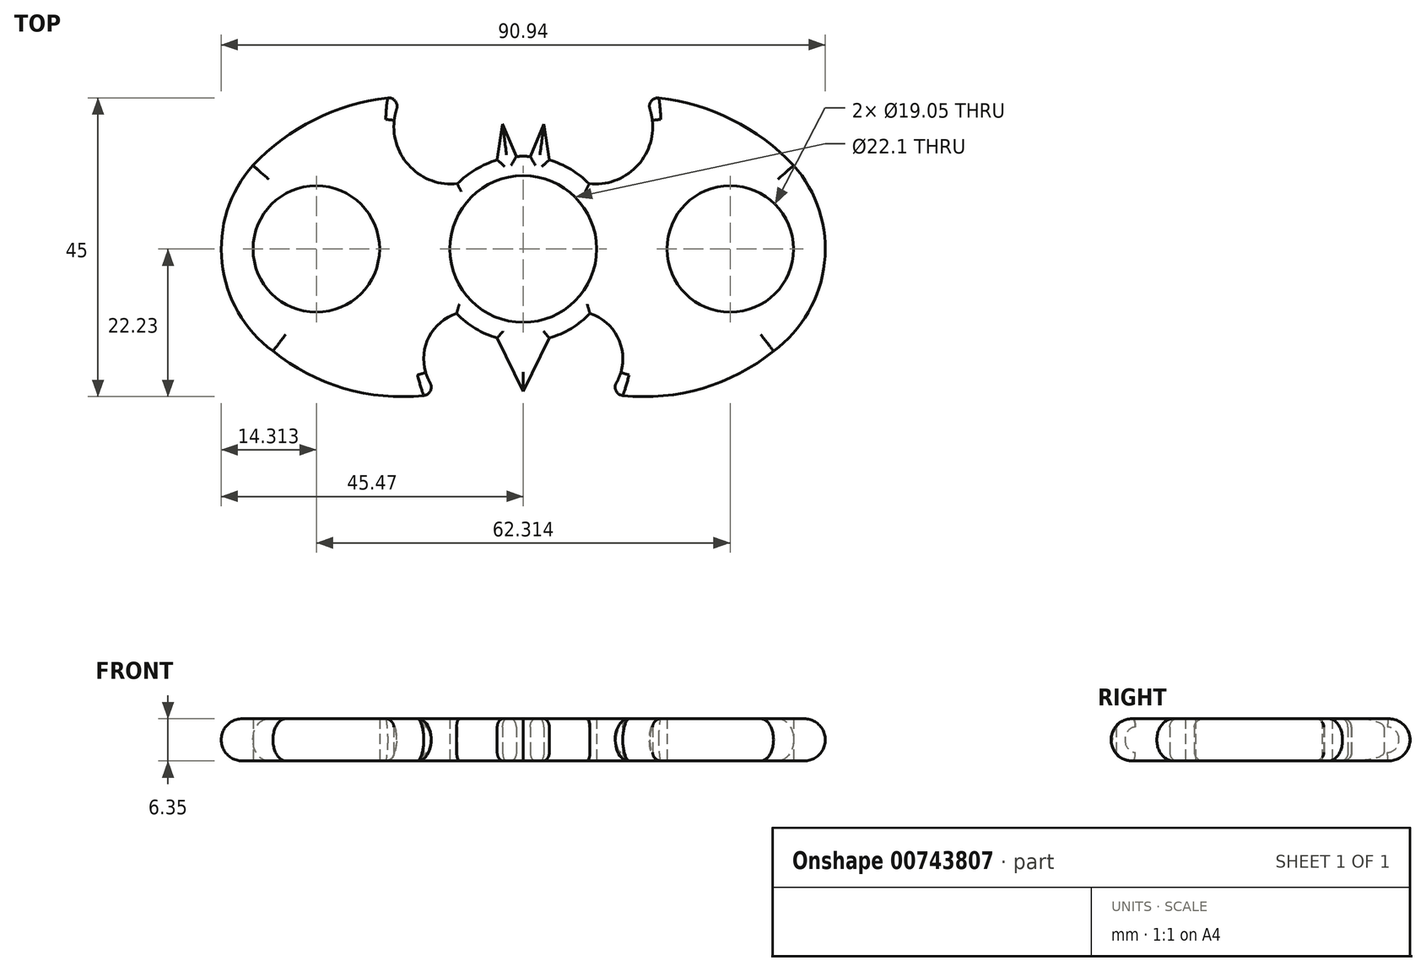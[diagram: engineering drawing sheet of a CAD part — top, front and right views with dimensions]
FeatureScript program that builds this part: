
annotation { "Feature Type Name" : "Feature", "Feature Type Description" : "" }
export const myFeature = defineFeature(function(context is Context, id is Id, definition is map)
    precondition{}
    {
        {
            var Q0;
            Q0=qCreatedBy(makeId("Top.planeOp"),FACE);
            var sketch = newSketch(context, id + "F0", { "sketchPlane" : qUnion([Q0])});
            skCircle(sketch, "E0", {"center": v(0, 0) * mm, "radius": 11.05 * mm});
            skCircle(sketch, "E1", {"center": v(0, 0) * mm, "radius": 13.97 * mm});
            skCircle(sketch, "E2", {"center": v(-31.16, 0) * mm, "radius": 9.53 * mm});
            skCircle(sketch, "E3", {"center": v(31.16, 0) * mm, "radius": 9.53 * mm});
            skArc(sketch, "E4", {"start": v(37.68, -15.37) * mm, "mid": v(45.36, -2.05) * mm, "end": v(40.7, 12.6) * mm});
            skArc(sketch, "E5", {"start": v(-18.2, 22.95) * mm, "mid": v(-30.45, 19.93) * mm, "end": v(-40.7, 12.6) * mm});
            skArc(sketch, "E6", {"start": v(-18.2, 22.95) * mm, "mid": v(-18.15, 13.81) * mm, "end": v(-9.93, 9.83) * mm});
            skArc(sketch, "E7.trimOffspring", {"start": v(-40.7, 12.6) * mm, "mid": v(-45.36, -2.05) * mm, "end": v(-37.68, -15.37) * mm});
            skArc(sketch, "E8.MirrorCS", {"start": v(18.2, 22.95) * mm, "mid": v(18.15, 13.81) * mm, "end": v(9.93, 9.83) * mm});
            skArc(sketch, "E9.MirrorCS", {"start": v(18.2, 22.95) * mm, "mid": v(30.45, 19.93) * mm, "end": v(40.7, 12.6) * mm});
            skArc(sketch, "E10", {"start": v(-37.68, -15.37) * mm, "mid": v(-25.91, -21.27) * mm, "end": v(-12.76, -21.74) * mm});
            skArc(sketch, "E11", {"start": v(-10.03, -9.72) * mm, "mid": v(-14.81, -14.95) * mm, "end": v(-12.76, -21.74) * mm});
            skArc(sketch, "E12.MirrorCS", {"start": v(10.03, -9.72) * mm, "mid": v(14.81, -14.95) * mm, "end": v(12.76, -21.74) * mm});
            skArc(sketch, "E13.MirrorCS", {"start": v(37.68, -15.37) * mm, "mid": v(25.91, -21.27) * mm, "end": v(12.76, -21.74) * mm});
            skPoint(sketch, "E14.end.orphan", {"position": v(2.34, 18.82) * mm});
            skPoint(sketch, "E15.orphan", {"position": v(3.92, 13.4) * mm});
            skPoint(sketch, "E16.end.orphan", {"position": v(-1.04, 13.93) * mm});
            skPoint(sketch, "E17.end.orphan", {"position": v(-2.23, 18.82) * mm});
            skPoint(sketch, "E18.MirrorCS.end.orphan", {"position": v(1.04, 13.93) * mm});
            skPoint(sketch, "E18.MirrorCS.start.orphan", {"position": v(2.23, 18.82) * mm});
            skPoint(sketch, "E19.end.orphan", {"position": v(-4.8, 18.35) * mm});
            skPoint(sketch, "E20.MirrorCS.end.orphan", {"position": v(4.8, 18.35) * mm});
            skLineSegment(sketch, "E21", {"start": v(-1.04, 13.93) * mm, "end": v(-3.1, 18.83) * mm});
            skLineSegment(sketch, "E22", {"start": v(-3.1, 18.83) * mm, "end": v(-3.92, 13.4) * mm});
            skLineSegment(sketch, "E23.MirrorCS", {"start": v(1.04, 13.93) * mm, "end": v(3.1, 18.83) * mm});
            skLineSegment(sketch, "E24.MirrorCS", {"start": v(3.1, 18.83) * mm, "end": v(3.92, 13.4) * mm});
            skPoint(sketch, "E25.end.orphan", {"position": v(0, -21.45) * mm});
            skPoint(sketch, "E25.start.orphan", {"position": v(-4.01, -13.38) * mm});
            skPoint(sketch, "E26.MirrorCS.start.orphan", {"position": v(4.01, -13.38) * mm});
            skPoint(sketch, "E27.MirrorCS.end.orphan", {"position": v(-3.92, -13.4) * mm});
            skPoint(sketch, "E27.MirrorCS.start.orphan", {"position": v(-3.1, -18.83) * mm});
            skLineSegment(sketch, "E28", {"start": v(-3.92, -13.4) * mm, "end": v(0, -21.45) * mm});
            skLineSegment(sketch, "E29.MirrorCS", {"start": v(3.92, -13.4) * mm, "end": v(0, -21.45) * mm});
            skLineSegment(sketch, "E30", {"start": v(-26.42, 0) * mm, "end": v(-31.16, 0) * mm});
            skLineSegment(sketch, "E31", {"start": v(26.42, 0) * mm, "end": v(31.16, 0) * mm});
            skSolve(sketch);
        }
        {
            var Q0;
            Q0=qSketchRegion(id+"F0",true);
            extrude(context, id + "F1", {"entities" : qUnion([Q0]), "depth" : 6.35 * mm, "offsetDistance" : 25.4 * mm});
        }
        {
            var Q0;
            Q0=makeQuery(id+"F1.opExtrude","CAP_EDGE",EDGE,{"disambiguationData":[OSD([sQuery(id+"F0.wireOp",EDGE,"E7.trimOffspring")])],"isStart":false});
            var Q1;
            Q1=makeQuery(id+"F1.opExtrude","CAP_EDGE",EDGE,{"disambiguationData":[OSD([sQuery(id+"F0.wireOp",EDGE,"E4")])],"isStart":false});
            var Q2;
            Q2=makeQuery(id+"F1.opExtrude","CAP_EDGE",EDGE,{"disambiguationData":[OSD([sQuery(id+"F0.wireOp",EDGE,"E4")])],"isStart":true});
            var Q3;
            Q3=makeQuery(id+"F1.opExtrude","CAP_EDGE",EDGE,{"disambiguationData":[OSD([sQuery(id+"F0.wireOp",EDGE,"E7.trimOffspring")])],"isStart":true});
            fillet(context, id + "F2", {"entities" : qUnion([Q0, Q1, Q2, Q3]), "radius" : 3.17 * mm, "tangentPropagation" : true, "allowEdgeOverflow" : false});
        }
        {
            var Q0;
            Q0=makeQuery(id+"F2.opFillet","BLEND_EDGE",EDGE,{"blendedFrom":[makeQuery(id+"F1.opExtrude","CAP_EDGE",EDGE,{"disambiguationData":[OSD([sQuery(id+"F0.wireOp",EDGE,"E7.trimOffspring")])],"isStart":false}),makeQuery(id+"F1.opExtrude","SWEPT_FACE",FACE,{"disambiguationData":[OSD([sQuery(id+"F0.wireOp",EDGE,"E6")])]})],"blendedInto":[makeQuery(id+"F1.opExtrude","SWEPT_FACE",FACE,{"disambiguationData":[OSD([sQuery(id+"F0.wireOp",EDGE,"E6")])]})]});
            var Q1;
            Q1=makeQuery(id+"F2.opFillet","BLEND_EDGE",EDGE,{"blendedFrom":[makeQuery(id+"F1.opExtrude","CAP_EDGE",EDGE,{"disambiguationData":[OSD([sQuery(id+"F0.wireOp",EDGE,"E7.trimOffspring")])],"isStart":true}),makeQuery(id+"F1.opExtrude","SWEPT_FACE",FACE,{"disambiguationData":[OSD([sQuery(id+"F0.wireOp",EDGE,"E6")])]})],"blendedInto":[makeQuery(id+"F1.opExtrude","SWEPT_FACE",FACE,{"disambiguationData":[OSD([sQuery(id+"F0.wireOp",EDGE,"E6")])]})]});
            var Q2;
            Q2=makeQuery(id+"F1.opExtrude","CAP_EDGE",EDGE,{"disambiguationData":[OSD([sQuery(id+"F0.wireOp",EDGE,"E11")])],"isStart":false});
            var Q3;
            Q3=makeQuery(id+"F1.opExtrude","CAP_EDGE",EDGE,{"disambiguationData":[OSD([sQuery(id+"F0.wireOp",EDGE,"E12.MirrorCS")])],"isStart":false});
            var Q4;
            Q4=makeQuery(id+"F1.opExtrude","CAP_EDGE",EDGE,{"disambiguationData":[OSD([sQuery(id+"F0.wireOp",EDGE,"E8.MirrorCS")])],"isStart":false});
            var Q5;
            {var subQ0=sQuery(id+"F0.wireOp",EDGE,"E1");Q5=makeQuery(id+"F1.opExtrude","CAP_EDGE",EDGE,{"disambiguationData":[OSD([subQ0]),TDD([makeQuery(id+"F0.imprint","IMPRINT",EDGE,{"disambiguationData":[TD([[makeQuery(id+"F0.imprint","INTERSECT",VERTEX,{"derivedFrom":[subQ0,sQuery(id+"F0.wireOp",EDGE,"E6")]}),1.0]])],"derivedFrom":subQ0})])],"isStart":false});}
            var Q6;
            Q6=makeQuery(id+"F1.opExtrude","CAP_EDGE",EDGE,{"disambiguationData":[OSD([sQuery(id+"F0.wireOp",EDGE,"E22")])],"isStart":false});
            var Q7;
            {var subQ0=sQuery(id+"F0.wireOp",EDGE,"E1");Q7=makeQuery(id+"F1.opExtrude","CAP_EDGE",EDGE,{"disambiguationData":[OSD([subQ0]),TDD([makeQuery(id+"F0.imprint","IMPRINT",EDGE,{"disambiguationData":[TD([[makeQuery(id+"F0.imprint","INTERSECT",VERTEX,{"derivedFrom":[subQ0,sQuery(id+"F0.wireOp",EDGE,"E21")]}),1.0]])],"derivedFrom":subQ0})])],"isStart":false});}
            var Q8;
            Q8=makeQuery(id+"F1.opExtrude","CAP_EDGE",EDGE,{"disambiguationData":[OSD([sQuery(id+"F0.wireOp",EDGE,"E23.MirrorCS")])],"isStart":false});
            var Q9;
            {var subQ0=sQuery(id+"F0.wireOp",EDGE,"E1");Q9=makeQuery(id+"F1.opExtrude","CAP_EDGE",EDGE,{"disambiguationData":[OSD([subQ0]),TDD([makeQuery(id+"F0.imprint","IMPRINT",EDGE,{"disambiguationData":[TD([[makeQuery(id+"F0.imprint","INTERSECT",VERTEX,{"derivedFrom":[subQ0,sQuery(id+"F0.wireOp",EDGE,"E8.MirrorCS")]}),-1.0]])],"derivedFrom":subQ0})])],"isStart":false});}
            var Q10;
            {var subQ0=sQuery(id+"F0.wireOp",EDGE,"E1");Q10=makeQuery(id+"F1.opExtrude","CAP_EDGE",EDGE,{"disambiguationData":[OSD([subQ0]),TDD([makeQuery(id+"F0.imprint","IMPRINT",EDGE,{"disambiguationData":[TD([[makeQuery(id+"F0.imprint","INTERSECT",VERTEX,{"derivedFrom":[subQ0,sQuery(id+"F0.wireOp",EDGE,"E8.MirrorCS")]}),-1.0]])],"derivedFrom":subQ0})])],"isStart":true});}
            var Q11;
            Q11=makeQuery(id+"F1.opExtrude","CAP_EDGE",EDGE,{"disambiguationData":[OSD([sQuery(id+"F0.wireOp",EDGE,"E24.MirrorCS")])],"isStart":true});
            var Q12;
            {var subQ0=sQuery(id+"F0.wireOp",EDGE,"E1");Q12=makeQuery(id+"F1.opExtrude","CAP_EDGE",EDGE,{"disambiguationData":[OSD([subQ0]),TDD([makeQuery(id+"F0.imprint","IMPRINT",EDGE,{"disambiguationData":[TD([[makeQuery(id+"F0.imprint","INTERSECT",VERTEX,{"derivedFrom":[subQ0,sQuery(id+"F0.wireOp",EDGE,"E21")]}),1.0]])],"derivedFrom":subQ0})])],"isStart":true});}
            var Q13;
            Q13=makeQuery(id+"F1.opExtrude","CAP_EDGE",EDGE,{"disambiguationData":[OSD([sQuery(id+"F0.wireOp",EDGE,"E21")])],"isStart":true});
            var Q14;
            Q14=makeQuery(id+"F1.opExtrude","CAP_EDGE",EDGE,{"disambiguationData":[OSD([sQuery(id+"F0.wireOp",EDGE,"E22")])],"isStart":true});
            var Q15;
            {var subQ0=sQuery(id+"F0.wireOp",EDGE,"E1");Q15=makeQuery(id+"F1.opExtrude","CAP_EDGE",EDGE,{"disambiguationData":[OSD([subQ0]),TDD([makeQuery(id+"F0.imprint","IMPRINT",EDGE,{"disambiguationData":[TD([[makeQuery(id+"F0.imprint","INTERSECT",VERTEX,{"derivedFrom":[subQ0,sQuery(id+"F0.wireOp",EDGE,"E6")]}),1.0]])],"derivedFrom":subQ0})])],"isStart":true});}
            var Q16;
            {var subQ0=sQuery(id+"F0.wireOp",EDGE,"E1");Q16=makeQuery(id+"F1.opExtrude","CAP_EDGE",EDGE,{"disambiguationData":[OSD([subQ0]),TDD([makeQuery(id+"F0.imprint","IMPRINT",EDGE,{"disambiguationData":[TD([[makeQuery(id+"F0.imprint","INTERSECT",VERTEX,{"derivedFrom":[subQ0,sQuery(id+"F0.wireOp",EDGE,"E11")]}),-1.0]])],"derivedFrom":subQ0})])],"isStart":false});}
            var Q17;
            Q17=makeQuery(id+"F1.opExtrude","CAP_EDGE",EDGE,{"disambiguationData":[OSD([sQuery(id+"F0.wireOp",EDGE,"E28")])],"isStart":false});
            var Q18;
            Q18=makeQuery(id+"F1.opExtrude","CAP_EDGE",EDGE,{"disambiguationData":[OSD([sQuery(id+"F0.wireOp",EDGE,"E29.MirrorCS")])],"isStart":false});
            var Q19;
            {var subQ0=sQuery(id+"F0.wireOp",EDGE,"E1");Q19=makeQuery(id+"F1.opExtrude","CAP_EDGE",EDGE,{"disambiguationData":[OSD([subQ0]),TDD([makeQuery(id+"F0.imprint","IMPRINT",EDGE,{"disambiguationData":[TD([[makeQuery(id+"F0.imprint","INTERSECT",VERTEX,{"derivedFrom":[subQ0,sQuery(id+"F0.wireOp",EDGE,"E12.MirrorCS")]}),1.0]])],"derivedFrom":subQ0})])],"isStart":false});}
            var Q20;
            {var subQ0=sQuery(id+"F0.wireOp",EDGE,"E1");Q20=makeQuery(id+"F1.opExtrude","CAP_EDGE",EDGE,{"disambiguationData":[OSD([subQ0]),TDD([makeQuery(id+"F0.imprint","IMPRINT",EDGE,{"disambiguationData":[TD([[makeQuery(id+"F0.imprint","INTERSECT",VERTEX,{"derivedFrom":[subQ0,sQuery(id+"F0.wireOp",EDGE,"E12.MirrorCS")]}),1.0]])],"derivedFrom":subQ0})])],"isStart":true});}
            var Q21;
            Q21=makeQuery(id+"F1.opExtrude","CAP_EDGE",EDGE,{"disambiguationData":[OSD([sQuery(id+"F0.wireOp",EDGE,"E29.MirrorCS")])],"isStart":true});
            var Q22;
            Q22=makeQuery(id+"F1.opExtrude","CAP_EDGE",EDGE,{"disambiguationData":[OSD([sQuery(id+"F0.wireOp",EDGE,"E28")])],"isStart":true});
            var Q23;
            {var subQ0=sQuery(id+"F0.wireOp",EDGE,"E1");Q23=makeQuery(id+"F1.opExtrude","CAP_EDGE",EDGE,{"disambiguationData":[OSD([subQ0]),TDD([makeQuery(id+"F0.imprint","IMPRINT",EDGE,{"disambiguationData":[TD([[makeQuery(id+"F0.imprint","INTERSECT",VERTEX,{"derivedFrom":[subQ0,sQuery(id+"F0.wireOp",EDGE,"E11")]}),-1.0]])],"derivedFrom":subQ0})])],"isStart":true});}
            var Q24;
            Q24=makeQuery(id+"F1.opExtrude","CAP_EDGE",EDGE,{"disambiguationData":[OSD([sQuery(id+"F0.wireOp",EDGE,"E23.MirrorCS")])],"isStart":true});
            var Q25;
            Q25=makeQuery(id+"F1.opExtrude","CAP_EDGE",EDGE,{"disambiguationData":[OSD([sQuery(id+"F0.wireOp",EDGE,"E24.MirrorCS")])],"isStart":false});
            var Q26;
            Q26=makeQuery(id+"F1.opExtrude","CAP_EDGE",EDGE,{"disambiguationData":[OSD([sQuery(id+"F0.wireOp",EDGE,"E21")])],"isStart":false});
            fillet(context, id + "F3", {"entities" : qUnion([Q0, Q1, Q2, Q3, Q4, Q5, Q6, Q7, Q8, Q9, Q10, Q11, Q12, Q13, Q14, Q15, Q16, Q17, Q18, Q19, Q20, Q21, Q22, Q23, Q24, Q25, Q26]), "radius" : 1.27 * mm, "tangentPropagation" : true, "allowEdgeOverflow" : false});
        }
    });
